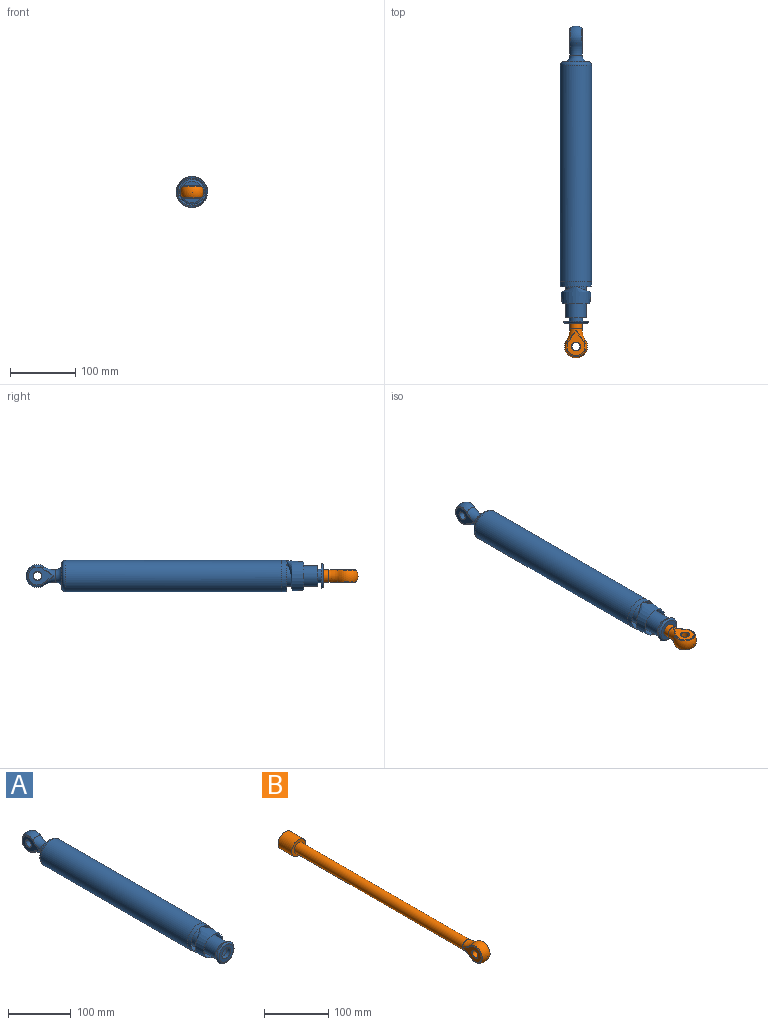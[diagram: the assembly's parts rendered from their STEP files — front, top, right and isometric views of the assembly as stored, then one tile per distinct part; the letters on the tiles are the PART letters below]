
ASSEMBLY  parts=2 mates=1
PART A: 22 faces, bbox 52.4x455.5x52.4 mm
  f0: sphere r=17.5mm, area 1341.6mm2, adj f1,f11,f13
  f1: torus R=39.48mm, axis (0,1,0), area 865.2mm2, adj f0,f12,f14,f20
  f2: plane 32x32mm, normal (0,-1,0), area 804.2mm2, adj f7
  f3: cylinder r=24mm len=330.85mm, axis (0,-1,0), area 49890.8mm2, adj f19,f21
  f4: plane 32.48x32.48mm, normal (0,-1,0), area 514.4mm2, adj f5,f18
  f5: cylinder r=10mm len=20mm, axis (0,-1,0), area 502.7mm2, adj f4,f6
  f6: plane 32x32mm, normal (0,1,0), area 490.1mm2, adj f5,f7
  f7: cylinder r=16mm len=384mm, axis (0,-1,0), area 38603.9mm2, adj f2,f6
  f8: plane 39.46x27.77mm, normal (-1,0,0), area 539.9mm2, adj f11,f12,f16
  f9: plane 39.46x27.77mm, normal (1,0,0), area 534.4mm2, adj f13,f14,f17
  f10: cylinder r=6.25mm len=18mm, axis (1,0,0), area 706.9mm2, adj f16,f17
  f11: cone r=13.66mm half-angle=59.6deg, axis (1,0,0), area 121.5mm2, adj f0,f8,f12
  f12: bspline ~23.52x16.66mm, area 42.7mm2, adj f1,f8,f11
  f13: cone r=15.26mm half-angle=59.6deg, axis (-1,0,0), area 121.5mm2, adj f0,f9,f14
  f14: bspline ~23.52x16.66mm, area 42.7mm2, adj f1,f9,f13
  f15: cone r=19mm half-angle=4.8deg, axis (0,1,0), area 7179.2mm2, adj f18,f19
  f16: cone r=6.75mm half-angle=45deg, axis (-1,0,0), area 28.9mm2, adj f8,f10
  f17: cone r=6.25mm half-angle=45deg, axis (1,0,0), area 28.9mm2, adj f9,f10
  f18: torus R=16.24mm, axis (0,1,0), area 507.2mm2, adj f4,f15
  f19: revolved ~48x48mm, area 1247.7mm2, adj f3,f15
  f20: torus R=19.5mm, axis (0,-1,0), area 1255.8mm2, adj f1,f21
  f21: torus R=19mm, axis (0,1,0), area 1074.7mm2, adj f3,f20
PART B: 15 faces, bbox 39.8x445.5x39.8 mm
  f0: torus R=39.48mm, axis (0,1,0), area 871.7mm2, adj f1,f5,f10,f12
  f1: sphere r=17.5mm, area 1341.6mm2, adj f0,f9,f11
  f2: plane 31x31mm, normal (0,1,0), area 754.8mm2, adj f3
  f3: cylinder r=15.5mm len=31mm, axis (0,-1,0), area 2921.7mm2, adj f2,f4
  f4: plane 31x31mm, normal (0,-1,0), area 471.2mm2, adj f3,f5
  f5: cylinder r=9.5mm len=370mm, axis (0,-1,0), area 22085.4mm2, adj f0,f4
  f6: plane 39.46x27.77mm, normal (1,0,0), area 538.4mm2, adj f11,f12,f14
  f7: plane 39.46x27.77mm, normal (-1,0,0), area 538.3mm2, adj f9,f10,f13
  f8: cylinder r=6.25mm len=18mm, axis (1,0,0), area 706.9mm2, adj f13,f14
  f9: cone r=15.26mm half-angle=59.6deg, axis (1,0,0), area 121.5mm2, adj f1,f7,f10
  f10: bspline ~23.52x16.66mm, area 42.7mm2, adj f0,f7,f9
  f11: cone r=13.66mm half-angle=59.6deg, axis (-1,0,0), area 121.5mm2, adj f1,f6,f12
  f12: bspline ~23.52x16.66mm, area 42.7mm2, adj f0,f6,f11
  f13: cone r=6.25mm half-angle=45deg, axis (-1,0,0), area 28.9mm2, adj f7,f8
  f14: cone r=6.25mm half-angle=45deg, axis (1,0,0), area 28.9mm2, adj f6,f8
PLACE A t=(62.12,-131.21,-40.11)mm fixed
PLACE B rot(axis=(0,-1,0),90deg) t=(62.12,-131.21,-40.11)mm
MATE slider A.f1 <-> B.f0  axis (0,-1,0) through (62.12,-131.21,-40.11)mm
